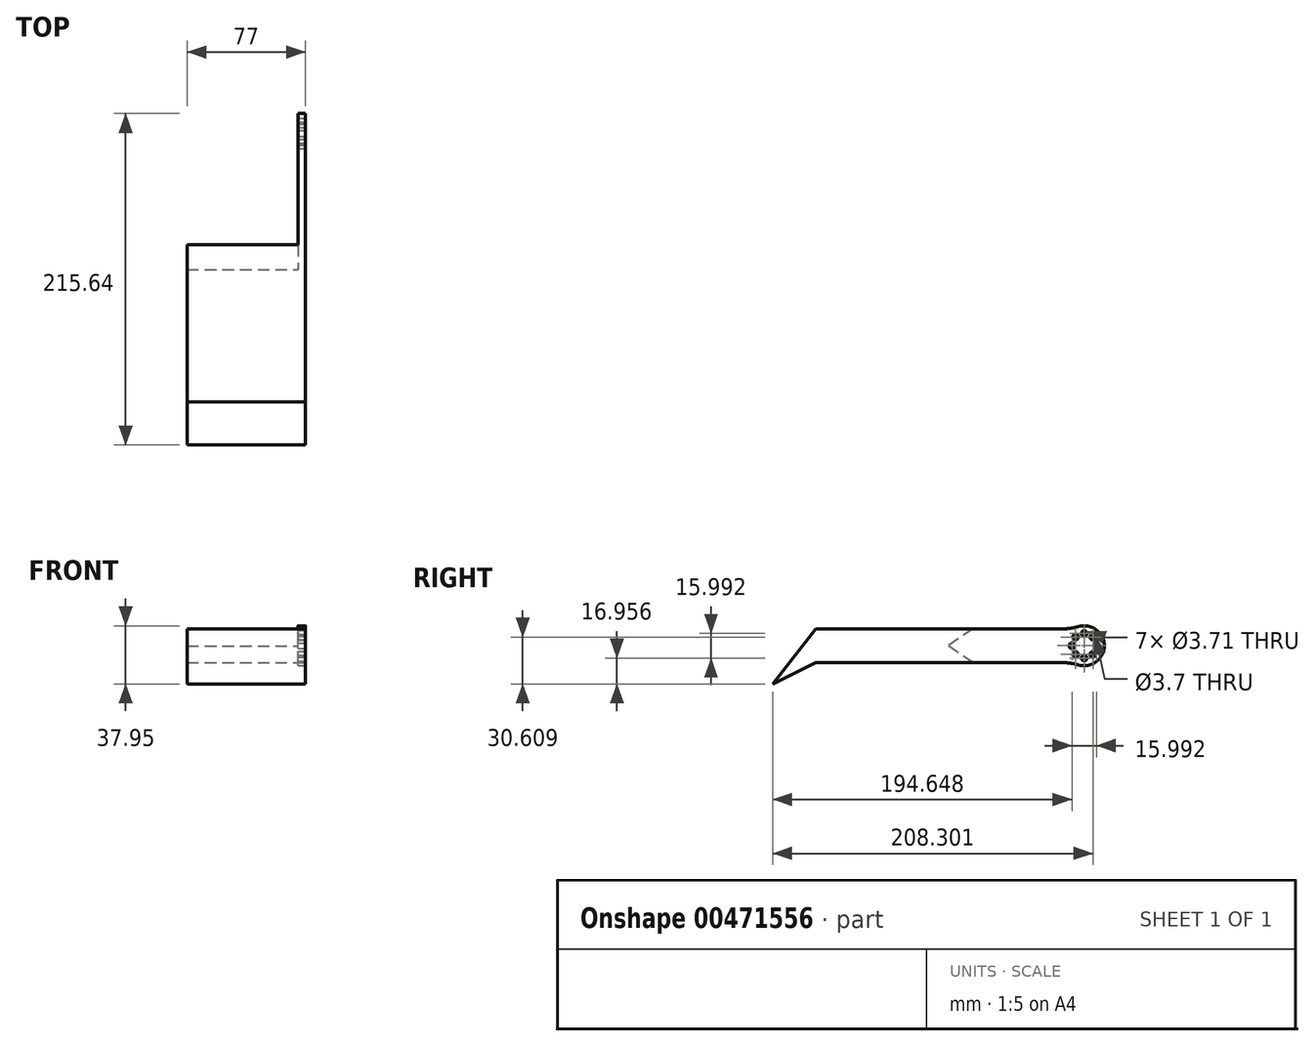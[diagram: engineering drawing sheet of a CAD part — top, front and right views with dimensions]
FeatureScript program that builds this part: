
annotation { "Feature Type Name" : "Feature", "Feature Type Description" : "" }
export const myFeature = defineFeature(function(context is Context, id is Id, definition is map)
    precondition{}
    {
        {
            var Q0;
            Q0=qCreatedBy(makeId("Right.planeOp"),FACE);
            var sketch = newSketch(context, id + "F0", { "sketchPlane" : qUnion([Q0])});
            skLineSegment(sketch, "E0", {"start": v(-42.2, 31.52) * mm, "end": v(60, 31.52) * mm});
            skLineSegment(sketch, "E1", {"start": v(-70.23, -4.43) * mm, "end": v(-42.2, 31.52) * mm});
            skLineSegment(sketch, "E2", {"start": v(-70.23, -4.43) * mm, "end": v(-42.2, 9.51) * mm});
            skLineSegment(sketch, "E3", {"start": v(-42.2, 9.51) * mm, "end": v(60.02, 9.51) * mm});
            skLineSegment(sketch, "E4", {"start": v(60, 31.52) * mm, "end": v(44.03, 20.52) * mm});
            skLineSegment(sketch, "E5", {"start": v(60.02, 9.51) * mm, "end": v(44.03, 20.52) * mm});
            skLineSegment(sketch, "E6", {"start": v(-42.2, 31.52) * mm, "end": v(-42.2, 9.51) * mm, "construction": true});
            skSolve(sketch);
        }
        {
            var Q0;
            Q0=qCreatedBy(makeId("Right.planeOp"),FACE);
            var sketch = newSketch(context, id + "F1", { "sketchPlane" : qUnion([Q0])});
            skLineSegment(sketch, "E7", {"start": v(60, 31.52) * mm, "end": v(125.49, 31.52) * mm});
            skLineSegment(sketch, "E8", {"start": v(125.5, 9.51) * mm, "end": v(60.02, 9.51) * mm});
            skLineSegment(sketch, "E9", {"start": v(60, 31.52) * mm, "end": v(44.03, 20.52) * mm});
            skLineSegment(sketch, "E10", {"start": v(60.02, 9.51) * mm, "end": v(44.03, 20.52) * mm});
            skCircle(sketch, "E11", {"center": v(132.41, 20.52) * mm, "radius": 13 * mm});
            skPoint(sketch, "E11.third.point", {"position": v(145.35, 21.86) * mm});
            skLineSegment(sketch, "E12", {"start": v(132.41, 51.7) * mm, "end": v(132.41, 20.52) * mm, "construction": true});
            skCircle(sketch, "E13", {"center": v(132.41, 28.52) * mm, "radius": 1.85 * mm});
            skPoint(sketch, "E13.first.point", {"position": v(132.41, 30.37) * mm});
            skPoint(sketch, "E13.second.point", {"position": v(132.41, 26.67) * mm});
            skPoint(sketch, "E13.third.point", {"position": v(134.26, 28.4) * mm});
            skLineSegment(sketch, "E14", {"start": v(132.41, 28.52) * mm, "end": v(132.41, 20.52) * mm, "construction": true});
            skLineSegment(sketch, "E15", {"start": v(132.41, 33.52) * mm, "end": v(132.41, 26.67) * mm, "construction": true});
            skLineSegment(sketch, "E16", {"start": v(132.41, 20.52) * mm, "end": v(132.41, 7.52) * mm, "construction": true});
            skCircle(sketch, "E17", {"center": v(132.41, 12.53) * mm, "radius": 1.85 * mm});
            skPoint(sketch, "E17.first.point", {"position": v(132.41, 14.38) * mm});
            skPoint(sketch, "E17.second.point", {"position": v(132.41, 10.67) * mm});
            skPoint(sketch, "E17.third.point", {"position": v(134.26, 12.65) * mm});
            skLineSegment(sketch, "E18", {"start": v(132.41, 14.38) * mm, "end": v(132.41, 12.53) * mm, "construction": true});
            skLineSegment(sketch, "E19", {"start": v(132.41, 14.38) * mm, "end": v(132.41, 7.52) * mm, "construction": true});
            skLineSegment(sketch, "E20", {"start": v(132.41, 20.52) * mm, "end": v(145.41, 20.52) * mm, "construction": true});
            skLineSegment(sketch, "E21", {"start": v(132.41, 20.52) * mm, "end": v(119.41, 20.52) * mm, "construction": true});
            skCircle(sketch, "E22", {"center": v(140.41, 20.52) * mm, "radius": 1.85 * mm});
            skPoint(sketch, "E22.first.point", {"position": v(138.56, 20.52) * mm});
            skPoint(sketch, "E22.second.point", {"position": v(142.26, 20.52) * mm});
            skPoint(sketch, "E22.third.point", {"position": v(140.32, 22.37) * mm});
            skLineSegment(sketch, "E23", {"start": v(140.41, 20.52) * mm, "end": v(132.41, 20.52) * mm, "construction": true});
            skLineSegment(sketch, "E24", {"start": v(138.56, 20.52) * mm, "end": v(145.41, 20.52) * mm, "construction": true});
            skCircle(sketch, "E25", {"center": v(124.42, 20.52) * mm, "radius": 1.85 * mm});
            skPoint(sketch, "E25.first.point", {"position": v(122.56, 20.52) * mm});
            skPoint(sketch, "E25.second.point", {"position": v(126.27, 20.52) * mm});
            skPoint(sketch, "E25.third.point", {"position": v(124.67, 22.36) * mm});
            skLineSegment(sketch, "E26", {"start": v(124.42, 20.52) * mm, "end": v(119.41, 20.52) * mm, "construction": true});
            skLineSegment(sketch, "E27", {"start": v(119.41, 20.52) * mm, "end": v(126.27, 20.52) * mm, "construction": true});
            skPoint(sketch, "E28.1.0", {"position": v(129.34, 25.84) * mm});
            skPoint(sketch, "E28.2.0", {"position": v(129.34, 15.2) * mm});
            skCircle(sketch, "E29.1.0", {"center": v(138.07, 26.18) * mm, "radius": 1.85 * mm});
            skLineSegment(sketch, "E29.anchor1", {"start": v(132.41, 20.52) * mm, "end": v(132.41, 28.52) * mm, "construction": true});
            skLineSegment(sketch, "E29.anchor2", {"start": v(132.41, 20.52) * mm, "end": v(140.41, 20.52) * mm, "construction": true});
            skCircle(sketch, "E30.1.0", {"center": v(138.07, 14.87) * mm, "radius": 1.85 * mm});
            skLineSegment(sketch, "E30.anchor2", {"start": v(132.41, 20.52) * mm, "end": v(132.41, 12.53) * mm, "construction": true});
            skCircle(sketch, "E31.1.0", {"center": v(126.76, 26.18) * mm, "radius": 1.85 * mm});
            skLineSegment(sketch, "E31.anchor1", {"start": v(132.41, 20.52) * mm, "end": v(124.42, 20.52) * mm, "construction": true});
            skCircle(sketch, "E32.1.0", {"center": v(126.76, 14.87) * mm, "radius": 1.85 * mm});
            skSolve(sketch);
        }
        {
            var Q0;
            Q0=makeQuery(id+"F0.imprint","IMPRINT",FACE,{"disambiguationData":[TD([[makeQuery(id+"F0.imprint","IMPRINT",EDGE,{"derivedFrom":sQuery(id+"F0.wireOp",EDGE,"E0")}),-1.0]])]});
            extrude(context, id + "F2", {"entities" : qUnion([Q0]), "oppositeDirection" : true, "depth" : 77 * mm});
        }
        {
            var Q0;
            {var subQ0=sQuery(id+"F1.wireOp",EDGE,"E11");var subQ1=makeQuery(id+"F1.imprint","INTERSECT",VERTEX,{"derivedFrom":[sQuery(id+"F1.wireOp",EDGE,"E7"),subQ0]});Q0=makeQuery(id+"F1.imprint","IMPRINT",FACE,{"disambiguationData":[TD([[makeQuery(id+"F1.imprint","IMPRINT",EDGE,{"disambiguationData":[TD([[subQ1,-1.0]])],"derivedFrom":subQ0}),1.0]])]});}
            var Q1;
            {var subQ1=sQuery(id+"F1.wireOp",EDGE,"E7");Q1=makeQuery(id+"F1.imprint","IMPRINT",FACE,{"disambiguationData":[TD([[makeQuery(id+"F1.imprint","IMPRINT",EDGE,{"derivedFrom":subQ1}),-1.0]])]});}
            extrude(context, id + "F3", {"entities" : qUnion([Q0, Q1]), "operationType" : NewBodyOperationType.ADD, "oppositeDirection" : true, "depth" : 5 * mm});
        }
        {
            var Q0;
            Q0=makeQuery(id+"F3.opExtrude","SWEPT_EDGE",EDGE,{"disambiguationData":[OSD([sQuery(id+"F1.wireOp",EDGE,"E7"),sQuery(id+"F1.wireOp",EDGE,"E11")])]});
            fillet(context, id + "F4", {"entities" : qUnion([Q0]), "radius" : 38.1 * mm, "tangentPropagation" : true, "allowEdgeOverflow" : false});
        }
        {
            var Q0;
            Q0=makeQuery(id+"F3.opExtrude","SWEPT_EDGE",EDGE,{"disambiguationData":[OSD([sQuery(id+"F1.wireOp",EDGE,"E8"),sQuery(id+"F1.wireOp",EDGE,"E11")])]});
            fillet(context, id + "F5", {"entities" : qUnion([Q0]), "radius" : 38.1 * mm, "tangentPropagation" : true, "allowEdgeOverflow" : false});
        }
    });
